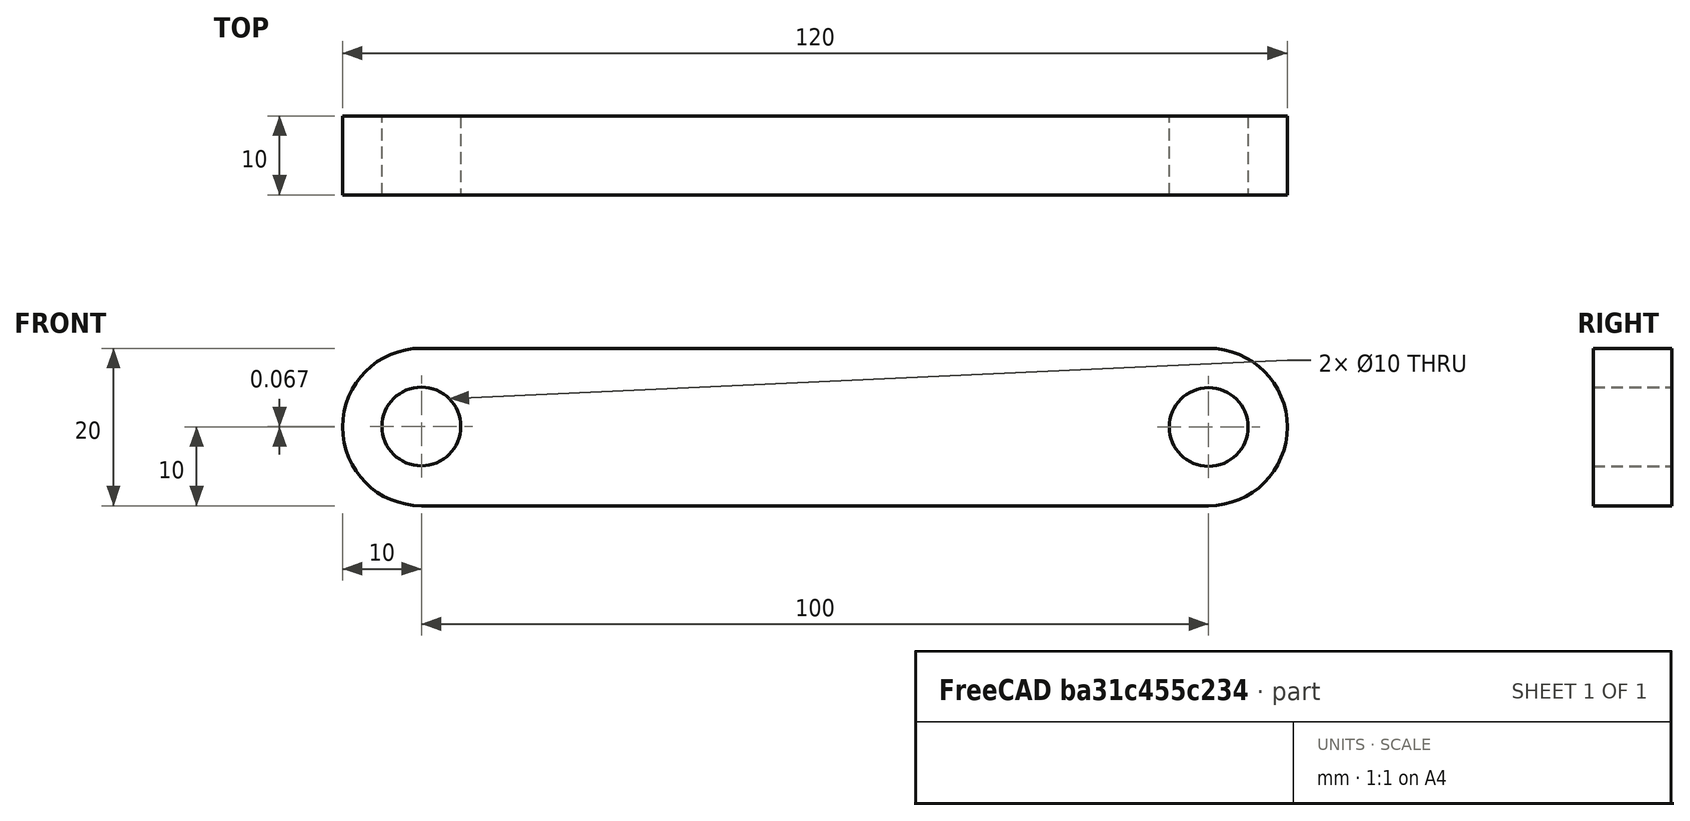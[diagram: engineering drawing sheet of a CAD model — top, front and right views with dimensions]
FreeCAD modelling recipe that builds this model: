
FCSTD DOCUMENT  (FreeCAD 0.21R33668 +26 (Git))
Label: Tuto1-002
License: All rights reserved
LicenseURL: http://en.wikipedia.org/wiki/All_rights_reserved
objects: PartDesign::CoordinateSystem×5, App::DocumentObjectGroup×3, Sketcher::SketchObject×2, App::Link×2, App::FeaturePython×1, PartDesign::Pad×1, PartDesign::Body×1, App::Part×1
note: 10 computed .brp shape members not serialized (recipe doc carries the construction recipe); baked Part::Feature solids carry a one-line shape summary decoded from their .brp

FEATURE [PartDesign::CoordinateSystem] LCS_Origin
  AttacherType = Attacher::AttachEngine3D
  MapMode = 2
  Support = -> [X_Axis]
FEATURE [App::DocumentObjectGroup] Constraints
FEATURE [App::FeaturePython] Variables  # WARN: FeaturePython — macro-defined, semantics opaque (R4)
  Type = App::PropertyContainer
  rotation_bielle1 = 79
FEATURE [App::DocumentObjectGroup] Configurations
FEATURE [Sketcher::SketchObject] Sketch_1
  FullyConstrained = true
  Support = -> [YZ_Plane]
  expr: Constraints[11] = Variables.rotation_bielle1
  sketch-geometry (3):
    g0: LineSegment StartX=90.2102 StartY=121.516 StartZ=0 EndX=1.29856 EndY=242.324 EndZ=0
    g1: LineSegment StartX=0 StartY=120 StartZ=0 EndX=19.0809 EndY=218.163 EndZ=0
    g2: LineSegment StartX=0 StartY=50 StartZ=0 EndX=72.4279 EndY=145.678 EndZ=0
  constraints (12):
    c: PointOnObject(g1,g0)
    c: PointOnObject(g2,g0)
    c: PointOnObject(g1,g-2)
    c: Distance(g1,g0) = 30
    c: Distance(g2,g0) = 30
    c: PointOnObject(g2,g-2)
    c: Distance(g2) = 120
    c: DistanceY(g-1,g1) = 120
    c: Distance(g1,g1) = 100
    c: Distance(g0) = 150
    c: DistanceY(g-1,g2) = 50
    c: Angle(g-1,g1) = 1.37881
FEATURE [PartDesign::CoordinateSystem] LCS_1
  AttacherType = Attacher::AttachEngine3D
  MapMode = 7
  Placement = pos=(0,120,0) rot=(0.990855,-0.095409,-0.095409;1.57998rad)
  Support = -> [Sketch_1]
FEATURE [PartDesign::CoordinateSystem] LCS_2
  AttacherType = Attacher::AttachEngine3D
  MapMode = 7
  Placement = pos=(90.2102,121.516,0) rot=(0.906999,0.297785,0.297785;1.66826rad)
  Support = -> [Sketch_1]
FEATURE [PartDesign::CoordinateSystem] LCS_3
  AttacherType = Attacher::AttachEngine3D
  MapMode = 7
  Placement = pos=(-3.6e-15,50,0) rot=(0.903307,-0.303345,-0.303345;1.67231rad)
  Support = -> [Sketch_1]
FEATURE [PartDesign::CoordinateSystem] LCS_0
  AttacherType = Attacher::AttachEngine3D
  MapMode = 2
  Support = -> [X_Axis001]
FEATURE [Sketcher::SketchObject] Sketch
  FullyConstrained = false
  MapMode = 5
  Placement = pos=(0,0,0) rot=(1,0,0;1.5708rad)
  Support = -> [XZ_Plane001]
  sketch-geometry (6):
    g0: ArcOfCircle CenterX=0 CenterY=0 CenterZ=0 NormalX=0 NormalY=0 NormalZ=1 AngleXU=0 Radius=10 StartAngle=1.5708 EndAngle=4.71239
    g1: ArcOfCircle CenterX=100 CenterY=1.1e-15 CenterZ=0 NormalX=0 NormalY=0 NormalZ=1 AngleXU=0 Radius=10 StartAngle=4.71239 EndAngle=7.85398
    g2: LineSegment StartX=-1.8e-15 StartY=-10 StartZ=0 EndX=100 EndY=-10 EndZ=0
    g3: LineSegment StartX=100 StartY=10 StartZ=0 EndX=7.958e-13 EndY=10 EndZ=0
    g4: Circle CenterX=100 CenterY=1.1e-15 CenterZ=0 NormalX=0 NormalY=0 NormalZ=1 AngleXU=0 Radius=5
    g5: Circle CenterX=0 CenterY=0.067016 CenterZ=0 NormalX=0 NormalY=0 NormalZ=1 AngleXU=0 Radius=5
  constraints (11):
    c: Tangent(g0,g2) = -1.5708
    c: Tangent(g2,g1) = -1.5708
    c: Tangent(g1,g3) = -1.5708
    c: Tangent(g3,g0) = -1.5708
    c: Equal(g0,g1)
    c: Horizontal(g2)
    c: Coincident(g0,g-1)
    c: Coincident(g4,g1)
    c: PointOnObject(g5,g-2)
    c: Radius(g5) = 5
    c: DistanceX(g5,g1) = 100
FEATURE [PartDesign::Pad] Pad
  Direction = (0,-1,-2e-16)
  Length = 10
  Length2 = 10
  Placement = pos=(0,0,0) rot=(1,0,0;1.5708rad)
  Profile = -> Sketch
  ReferenceAxis = -> Sketch [N_Axis]
  Type = 0
FEATURE [PartDesign::Body] Body
  Group = -> [LCS_0,Sketch,Pad]
  Origin = -> Origin001
  Tip = -> Pad
FEATURE [App::DocumentObjectGroup] Parts
  Group = -> [Body]
FEATURE [App::Link] Body001
  AttachedBy = #LCS_0
  AttachedTo = Parent Assembly#LCS_1
  AttachmentOffset = pos=(0,0,0) rot=(-0.707107,0,0.707107;3.14159rad)
  LinkPlacement = pos=(0,120,0) rot=(-0.651074,-0.536704,0.536704;1.98733rad)
  LinkedObject = -> Body
  Placement = pos=(0,120,0) rot=(-0.651074,-0.536704,0.536704;1.98733rad)
  SolverId = Asm4EE
  expr: Placement = LCS_1.Placement * AttachmentOffset * LCS_0.Placement ^ -1
FEATURE [App::Link] Body002
  AttachedBy = #LCS_0
  AttachedTo = Parent Assembly#LCS_3
  AttachmentOffset = pos=(0,0,0) rot=(-0.707107,0,0.707107;3.14159rad)
  LinkPlacement = pos=(-3.6e-15,50,0) rot=(-0.818014,-0.406727,0.406727;1.77033rad)
  LinkedObject = -> Body
  Placement = pos=(-3.6e-15,50,0) rot=(-0.818014,-0.406727,0.406727;1.77033rad)
  SolverId = Asm4EE
  expr: Placement = LCS_3.Placement * AttachmentOffset * LCS_0.Placement ^ -1
FEATURE [App::Part] Assembly
  AssemblyType = Part::Link
  Group = -> [LCS_Origin,Constraints,Variables,Configurations,Sketch_1,LCS_1,LCS_2,LCS_3,Body001,Body002]
  Origin = -> Origin
  Type = Assembly
